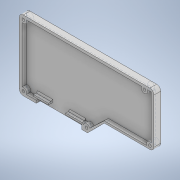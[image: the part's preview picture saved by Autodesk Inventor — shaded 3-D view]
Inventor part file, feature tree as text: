
AUTODESK INVENTOR PART (.ipt)
format: ipt  version: 2021 (Build 250183000, 183)  size: 287,744 bytes
history: native  units: mm
features: sketch x11, extrude x10, fillet x2, hole x1, chamfer x1
ambient origin geometry x8: Origin, YZ Plane, XZ Plane, XY Plane, X Axis, Y Axis, Z Axis, Center Point
bodies: Solid1 (feature_tree)
feature tree (25):
  extrude  "Extrusion1"  Depth=100.0mm
  extrude  "Extrusion2"  Depth=50.0mm
  hole  "Hole1"  [1 undecoded]
  extrude  "Extrusion3"  Depth=50.0mm
  extrude  "Extrusion4"  Depth=3.0mm
  extrude  "Extrusion5"  Depth=3.0mm
  fillet  "Fillet1"  Radius=49.0mm
  extrude  "Extrusion6"  Depth=49.0mm
  extrude  "Extrusion7"  Depth=5.0mm
  extrude  "Extrusion8"  Depth=5.0mm
  chamfer  "Chamfer1"  Distance=2.0mm
  extrude  "Extrusion9"  Depth=5.0mm
  fillet  "Fillet2"  Radius=2.0mm
  extrude  "Extrusion11"  Depth=5.0mm
  sketch  "Sketch1"  dims[d0=52.0mm d1=100.0mm]
  sketch  "Sketch2"  dims[d2=26.0mm d3=50.0mm]
  sketch  "Sketch3"  dims[d4=2.0mm d5=0.0mm d6=3.0mm]
  sketch  "Sketch4"  dims[d7=3.0mm d8=50.0mm]
  sketch  "Sketch5"  dims[d9=3.0mm d10=97.0mm]
  sketch  "Sketch6"  dims[d11=15.0mm d12=3.0mm d13=49.0mm]
  sketch  "Sketch7"  dims[d14=93.0mm d15=49.0mm]
  sketch  "Sketch8"  dims[d16=2.0mm d17=5.0mm]
  sketch  "Sketch9"  dims[d18=2.0mm d19=5.0mm]
  sketch  "Sketch10"  dims[d20=2.0mm]
  sketch  "Sketch12"  dims[d21=5.0mm d22=2.0mm d23=5.0mm d24=2.0mm d25=5.0mm d26=3.0mm d27=0.0mm d28=2.0mm d29=6.0mm d30=5.0mm d31=2.0mm d32=90.0deg d33=10.0mm d34=20.594885mm d35=12.5mm d36=63.1mm d37=3.0mm d38=0.0mm d39=50.673mm d40=3.0mm d41=0.0mm d42=2.0mm d43=2.0mm d44=2.0mm d45=1.5mm d46=3.0mm d47=0.0mm d48=3.0mm d49=7.6mm d50=46.4mm d51=6.7mm d52=3.0mm d53=0.0mm d54=5.0mm d55=2.0mm d56=12.0mm d57=0.0mm d58=1.4mm d59=1.2mm d60=3.0mm d61=14.0mm d62=1.2mm d63=1.4mm d64=12.0mm d65=3.0mm d66=0.0mm d67=1.0mm d68=2.0mm d69=45.0deg d70=1.2mm d71=3.0mm d72=0.0mm d73=1.0mm d77=3.0mm d78=0.0mm d74=0.872665mm d75=0.872665mm d76=0.5mm]
note: 1 required parameter value undecoded (feature->parameter linkage not recoverable at this tier; creation-order binding heuristic only, values carry confidence <= 0.55)
